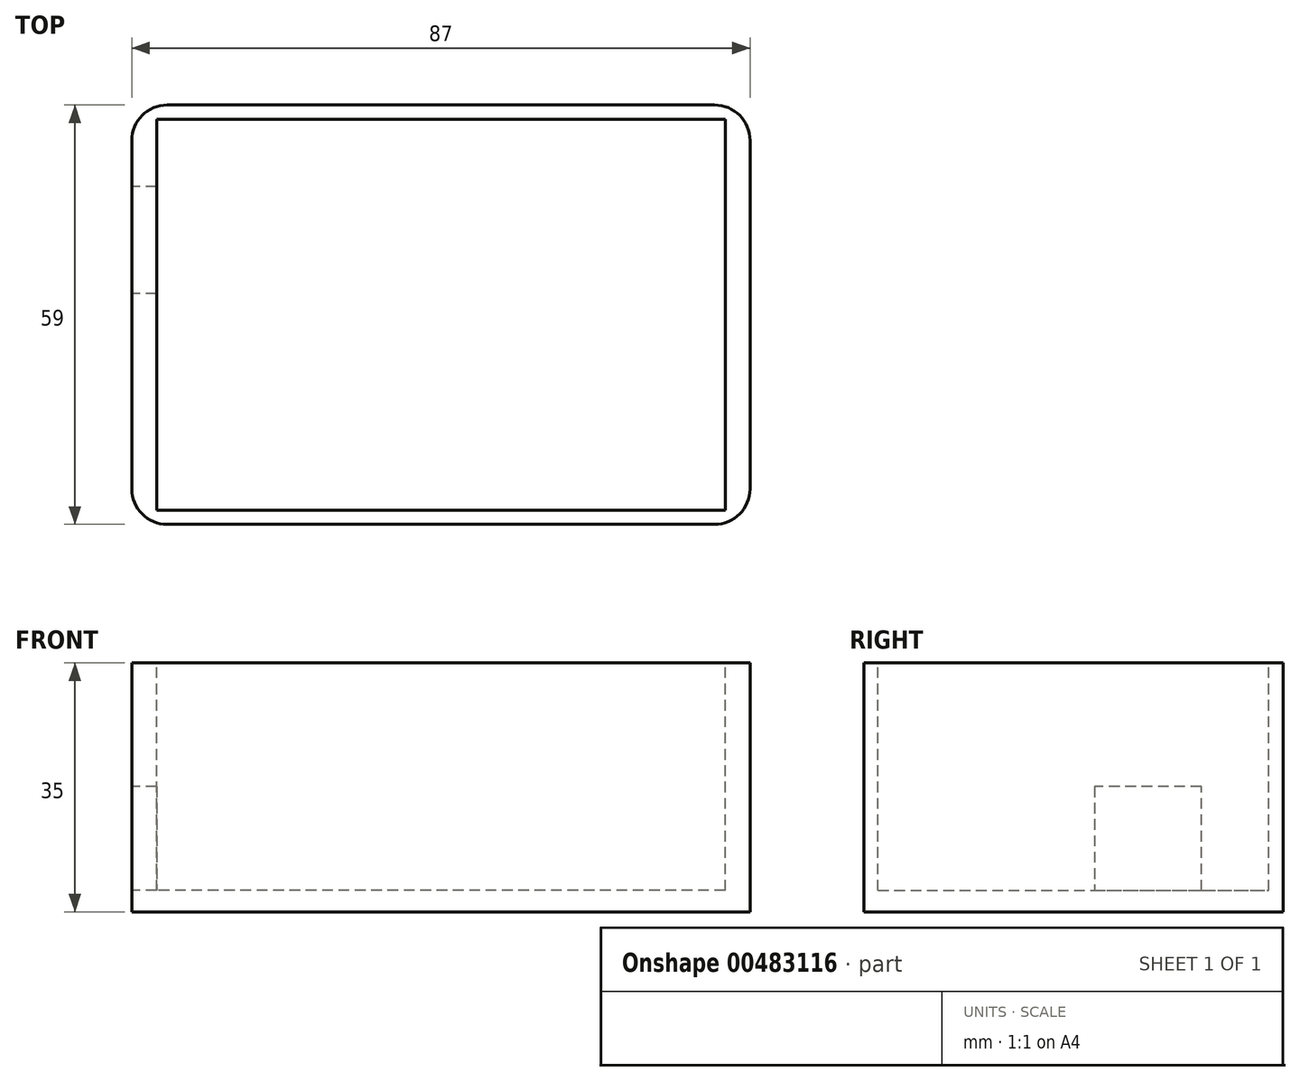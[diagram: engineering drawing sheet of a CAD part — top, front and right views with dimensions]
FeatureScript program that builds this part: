
annotation { "Feature Type Name" : "Feature", "Feature Type Description" : "" }
export const myFeature = defineFeature(function(context is Context, id is Id, definition is map)
    precondition{}
    {
        {
            var Q0;
            Q0=qCreatedBy(makeId("Top.planeOp"),FACE);
            var sketch = newSketch(context, id + "F0", { "sketchPlane" : qUnion([Q0])});
            skLineSegment(sketch, "E0.bottom", {"start": v(43.5, -29.5) * mm, "end": v(-43.5, -29.5) * mm});
            skLineSegment(sketch, "E0.top", {"start": v(43.5, 29.5) * mm, "end": v(-43.5, 29.5) * mm});
            skLineSegment(sketch, "E0.left", {"start": v(43.5, -29.5) * mm, "end": v(43.5, 29.5) * mm});
            skLineSegment(sketch, "E0.right", {"start": v(-43.5, -29.5) * mm, "end": v(-43.5, 29.5) * mm});
            skPoint(sketch, "E0.middle", {"position": v(0, 0) * mm});
            skSolve(sketch);
        }
        {
            var Q0;
            Q0 = qSketchRegion(id + "F0", true);
            extrude(context, id + "F1", {"entities" : qUnion([Q0]), "depth" : 35 * mm});
        }
        {
            var Q0;
            Q0=makeQuery(id+"F1.opExtrude","CAP_FACE",FACE,{"disambiguationData":[OSD([sQuery(id+"F0.wireOp",EDGE,"E0.bottom"),sQuery(id+"F0.wireOp",EDGE,"E0.top"),sQuery(id+"F0.wireOp",EDGE,"E0.left"),sQuery(id+"F0.wireOp",EDGE,"E0.right")])],"isStart":false});
            var sketch = newSketch(context, id + "F2", { "sketchPlane" : qUnion([Q0])});
            skLineSegment(sketch, "E1", {"start": v(-43.5, 0) * mm, "end": v(43.5, 0) * mm});
            skLineSegment(sketch, "E2", {"start": v(0, 29.5) * mm, "end": v(0, -29.5) * mm});
            skLineSegment(sketch, "E3.bottom", {"start": v(40, -27.5) * mm, "end": v(-40, -27.5) * mm});
            skLineSegment(sketch, "E3.top", {"start": v(40, 27.5) * mm, "end": v(-40, 27.5) * mm});
            skLineSegment(sketch, "E3.left", {"start": v(40, -27.5) * mm, "end": v(40, 27.5) * mm});
            skLineSegment(sketch, "E3.right", {"start": v(-40, -27.5) * mm, "end": v(-40, 27.5) * mm});
            skPoint(sketch, "E3.middle", {"position": v(0, 0) * mm});
            skSolve(sketch);
        }
        {
            var Q0;
            {var subQ0=sQuery(id+"F2.wireOp",EDGE,"E3.right");var subQ1=sQuery(id+"F2.wireOp",EDGE,"E1");var subQ2=makeQuery(id+"F2.imprint","INTERSECT",VERTEX,{"derivedFrom":[subQ1,subQ0]});Q0=makeQuery(id+"F2.imprint","IMPRINT",FACE,{"disambiguationData":[TD([[makeQuery(id+"F2.imprint","IMPRINT",EDGE,{"disambiguationData":[TD([[subQ2,-1.0]])],"derivedFrom":subQ1}),-1.0]])]});}
            var Q1;
            {var subQ0=sQuery(id+"F2.wireOp",EDGE,"E2");var subQ1=sQuery(id+"F2.wireOp",EDGE,"E1");var subQ2=makeQuery(id+"F2.imprint","INTERSECT",VERTEX,{"derivedFrom":[subQ1,subQ0]});Q1=makeQuery(id+"F2.imprint","IMPRINT",FACE,{"disambiguationData":[TD([[makeQuery(id+"F2.imprint","IMPRINT",EDGE,{"disambiguationData":[TD([[subQ2,-1.0]])],"derivedFrom":subQ1}),1.0]])]});}
            var Q2;
            {var subQ0=sQuery(id+"F2.wireOp",EDGE,"E2");var subQ1=sQuery(id+"F2.wireOp",EDGE,"E1");var subQ2=makeQuery(id+"F2.imprint","INTERSECT",VERTEX,{"derivedFrom":[subQ1,subQ0]});Q2=makeQuery(id+"F2.imprint","IMPRINT",FACE,{"disambiguationData":[TD([[makeQuery(id+"F2.imprint","IMPRINT",EDGE,{"disambiguationData":[TD([[subQ2,-1.0]])],"derivedFrom":subQ1}),-1.0]])]});}
            var Q3;
            {var subQ0=sQuery(id+"F2.wireOp",EDGE,"E3.right");var subQ1=sQuery(id+"F2.wireOp",EDGE,"E1");var subQ2=makeQuery(id+"F2.imprint","INTERSECT",VERTEX,{"derivedFrom":[subQ1,subQ0]});Q3=makeQuery(id+"F2.imprint","IMPRINT",FACE,{"disambiguationData":[TD([[makeQuery(id+"F2.imprint","IMPRINT",EDGE,{"disambiguationData":[TD([[subQ2,-1.0]])],"derivedFrom":subQ1}),1.0]])]});}
            extrude(context, id + "F3", {"entities" : qUnion([Q0, Q1, Q2, Q3]), "operationType" : NewBodyOperationType.REMOVE, "oppositeDirection" : true, "depth" : 32 * mm});
        }
        {
            var Q0;
            Q0=makeQuery(id+"F1.opExtrude","SWEPT_EDGE",EDGE,{"disambiguationData":[OSD([sQuery(id+"F0.wireOp",EDGE,"E0.bottom"),sQuery(id+"F0.wireOp",EDGE,"E0.right")])]});
            var Q1;
            Q1=makeQuery(id+"F1.opExtrude","SWEPT_EDGE",EDGE,{"disambiguationData":[OSD([sQuery(id+"F0.wireOp",EDGE,"E0.bottom"),sQuery(id+"F0.wireOp",EDGE,"E0.left")])]});
            var Q2;
            Q2=makeQuery(id+"F1.opExtrude","SWEPT_EDGE",EDGE,{"disambiguationData":[OSD([sQuery(id+"F0.wireOp",EDGE,"E0.top"),sQuery(id+"F0.wireOp",EDGE,"E0.left")])]});
            var Q3;
            Q3=makeQuery(id+"F1.opExtrude","SWEPT_EDGE",EDGE,{"disambiguationData":[OSD([sQuery(id+"F0.wireOp",EDGE,"E0.top"),sQuery(id+"F0.wireOp",EDGE,"E0.right")])]});
            fillet(context, id + "F4", {"entities" : qUnion([Q0, Q1, Q2, Q3]), "radius" : 5 * mm, "tangentPropagation" : true, "allowEdgeOverflow" : false});
        }
        {
            var Q0;
            Q0=makeQuery(id+"F1.opExtrude","SWEPT_FACE",FACE,{"disambiguationData":[OSD([sQuery(id+"F0.wireOp",EDGE,"E0.right")])]});
            var sketch = newSketch(context, id + "F5", { "sketchPlane" : qUnion([Q0])});
            skLineSegment(sketch, "E4", {"start": v(-27.5, 11.94) * mm, "end": v(-34.5, 11.94) * mm});
            skPoint(sketch, "E5", {"position": v(-34.5, 11.94) * mm});
            skLineSegment(sketch, "E6", {"start": v(24.08, 3) * mm, "end": v(-25.03, 3) * mm});
            skPoint(sketch, "E7.endSnap0", {"position": v(0, 3) * mm});
            skLineSegment(sketch, "E8", {"start": v(-34.5, 7) * mm, "end": v(-34.5, 3) * mm});
            skLineSegment(sketch, "E9", {"start": v(-49.5, 7) * mm, "end": v(-49.5, 3) * mm});
            skLineSegment(sketch, "E10", {"start": v(-49.5, 3) * mm, "end": v(-49.5, 17) * mm});
            skLineSegment(sketch, "E11", {"start": v(-49.5, 17) * mm, "end": v(-34.5, 17) * mm});
            skLineSegment(sketch, "E12", {"start": v(-34.5, 17) * mm, "end": v(-34.5, 3) * mm});
            skLineSegment(sketch, "E13", {"start": v(-34.5, 3) * mm, "end": v(-49.5, 3) * mm});
            skLineSegment(sketch, "E14", {"start": v(-24.5, 5.2) * mm, "end": v(-18, 5.2) * mm});
            skLineSegment(sketch, "E15", {"start": v(-18, 5.2) * mm, "end": v(-3, 5.2) * mm});
            skLineSegment(sketch, "E16", {"start": v(-18, 3) * mm, "end": v(-18, 17.63) * mm});
            skLineSegment(sketch, "E17", {"start": v(-18, 17.63) * mm, "end": v(-3, 17.63) * mm});
            skLineSegment(sketch, "E18", {"start": v(-3, 17.63) * mm, "end": v(-3, 3) * mm});
            skSolve(sketch);
        }
        {
            var Q0;
            {var subQ0=sQuery(id+"F5.wireOp",EDGE,"E15");Q0=makeQuery(id+"F5.imprint","IMPRINT",FACE,{"disambiguationData":[TD([[makeQuery(id+"F5.imprint","IMPRINT",EDGE,{"derivedFrom":subQ0}),1.0]])]});}
            var Q1;
            {var subQ5=sQuery(id+"F5.wireOp",EDGE,"E15");Q1=makeQuery(id+"F5.imprint","IMPRINT",FACE,{"disambiguationData":[TD([[makeQuery(id+"F5.imprint","IMPRINT",EDGE,{"derivedFrom":subQ5}),-1.0]])]});}
            extrude(context, id + "F6", {"entities" : qUnion([Q0, Q1]), "operationType" : NewBodyOperationType.REMOVE, "oppositeDirection" : true, "depth" : 25 * mm});
        }
    });
